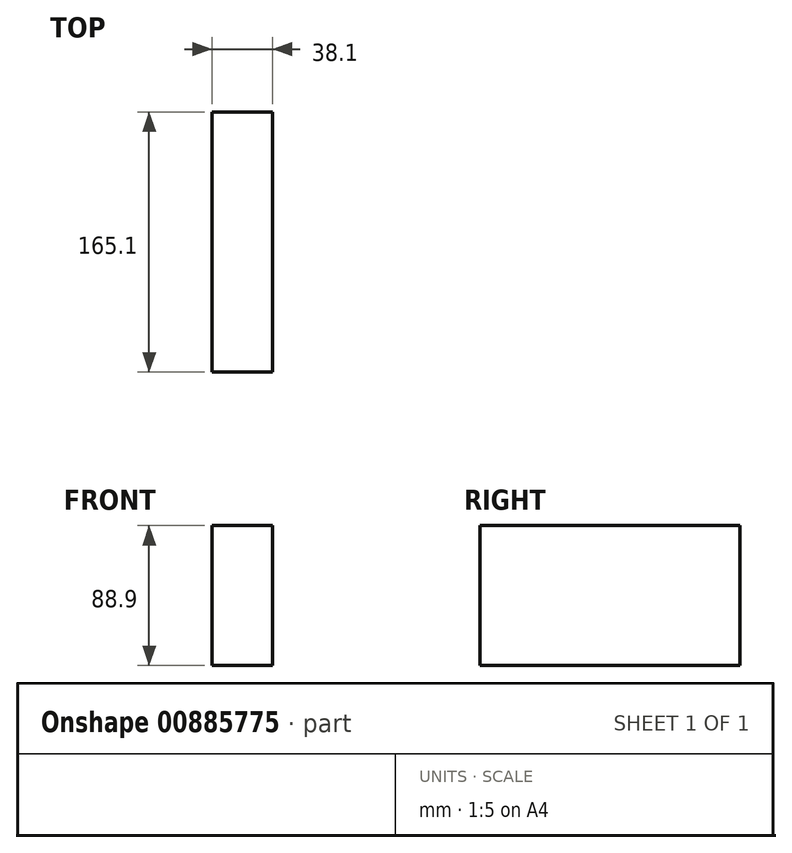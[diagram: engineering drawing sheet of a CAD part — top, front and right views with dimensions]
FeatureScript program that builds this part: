
annotation { "Feature Type Name" : "Feature", "Feature Type Description" : "" }
export const myFeature = defineFeature(function(context is Context, id is Id, definition is map)
    precondition{}
    {
        {
            var Q0;
            Q0=qCreatedBy(makeId("Front.planeOp"),FACE);
            var sketch = newSketch(context, id + "F0", { "sketchPlane" : qUnion([Q0])});
            skLineSegment(sketch, "E0.bottom", {"start": v(19.05, -44.45) * mm, "end": v(-19.05, -44.45) * mm});
            skLineSegment(sketch, "E0.top", {"start": v(19.05, 44.45) * mm, "end": v(-19.05, 44.45) * mm});
            skLineSegment(sketch, "E0.left", {"start": v(19.05, -44.45) * mm, "end": v(19.05, 44.45) * mm});
            skLineSegment(sketch, "E0.right", {"start": v(-19.05, -44.45) * mm, "end": v(-19.05, 44.45) * mm});
            skPoint(sketch, "E0.middle", {"position": v(0, 0) * mm});
            skSolve(sketch);
        }
        {
            var Q0;
            Q0=makeQuery(id+"F0.imprint","IMPRINT",FACE,{"disambiguationData":[TD([[makeQuery(id+"F0.imprint","IMPRINT",EDGE,{"derivedFrom":sQuery(id+"F0.wireOp",EDGE,"E0.bottom")}),-1.0]])]});
            extrude(context, id + "F1", {"entities" : qUnion([Q0]), "endBound" : BoundingType.SYMMETRIC, "depth" : 165.1 * mm, "offsetDistance" : 25.4 * mm});
        }
    });
